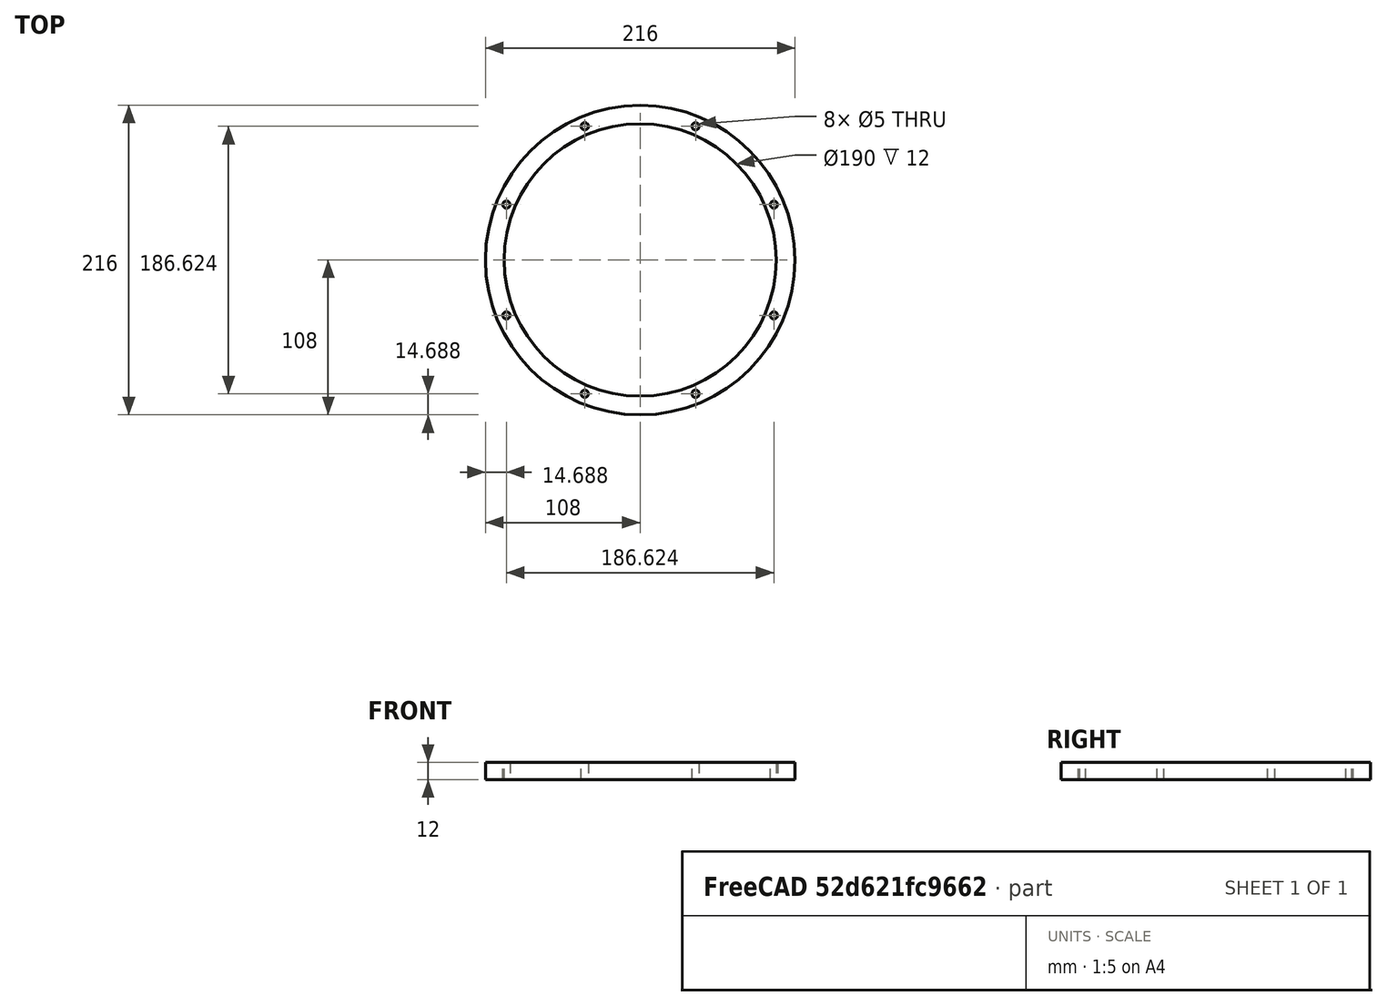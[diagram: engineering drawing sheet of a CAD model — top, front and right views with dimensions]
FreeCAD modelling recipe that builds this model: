
FCSTD DOCUMENT  (FreeCAD 0.19R24276 (Git))
Label: Out_gear_holder_for_CNC_H12_middle_parts
License: All rights reserved
LicenseURL: http://en.wikipedia.org/wiki/All_rights_reserved
objects: Sketcher::SketchObject×1, PartDesign::Pad×1, PartDesign::Body×1
note: 4 computed .brp shape members not serialized (recipe doc carries the construction recipe); baked Part::Feature solids carry a one-line shape summary decoded from their .brp

FEATURE [Sketcher::SketchObject] Sketch001  label="Sketch001_d190_d216"
  FullyConstrained = false
  MapMode = 5
  Placement = pos=(0,0,0) rot=(1,0,0;3.14159rad)
  sketch-geometry (20):
    g0: Circle CenterX=0 CenterY=0 CenterZ=0 NormalX=0 NormalY=0 NormalZ=1 AngleXU=0 Radius=95
    g1: Circle CenterX=0 CenterY=0 CenterZ=0 NormalX=0 NormalY=0 NormalZ=1 AngleXU=0 Radius=95
    g2: Circle CenterX=0 CenterY=0 CenterZ=0 NormalX=0 NormalY=0 NormalZ=1 AngleXU=0 Radius=108
    g3: Circle CenterX=0 CenterY=0 CenterZ=0 NormalX=0 NormalY=0 NormalZ=1 AngleXU=0 Radius=101
    g4: LineSegment StartX=0 StartY=0 StartZ=0 EndX=93.3118 EndY=38.651 EndZ=0
    g5: LineSegment StartX=0 StartY=0 StartZ=0 EndX=-93.3118 EndY=38.651 EndZ=0
    g6: LineSegment StartX=0 StartY=0 StartZ=0 EndX=-93.3118 EndY=-38.651 EndZ=0
    g7: LineSegment StartX=0 StartY=0 StartZ=0 EndX=38.651 EndY=93.3118 EndZ=0
    g8: LineSegment StartX=0 StartY=0 StartZ=0 EndX=-38.651 EndY=-93.3118 EndZ=0
    g9: LineSegment StartX=0 StartY=0 StartZ=0 EndX=-38.651 EndY=93.3118 EndZ=0
    g10: LineSegment StartX=0 StartY=0 StartZ=0 EndX=38.651 EndY=-93.3118 EndZ=0
    g11: LineSegment StartX=0 StartY=0 StartZ=0 EndX=93.3118 EndY=-38.651 EndZ=0
    g12: Circle CenterX=38.651 CenterY=93.3118 CenterZ=0 NormalX=0 NormalY=0 NormalZ=1 AngleXU=0 Radius=2.5
    g13: Circle CenterX=93.3118 CenterY=38.651 CenterZ=0 NormalX=0 NormalY=0 NormalZ=1 AngleXU=0 Radius=2.5
    g14: Circle CenterX=93.3118 CenterY=-38.651 CenterZ=0 NormalX=0 NormalY=0 NormalZ=1 AngleXU=0 Radius=2.5
    g15: Circle CenterX=38.651 CenterY=-93.3118 CenterZ=0 NormalX=0 NormalY=0 NormalZ=1 AngleXU=0 Radius=2.5
    g16: Circle CenterX=-38.651 CenterY=93.3118 CenterZ=0 NormalX=0 NormalY=0 NormalZ=1 AngleXU=0 Radius=2.5
    g17: Circle CenterX=-93.3118 CenterY=38.651 CenterZ=0 NormalX=0 NormalY=0 NormalZ=1 AngleXU=0 Radius=2.5
    g18: Circle CenterX=-93.3118 CenterY=-38.651 CenterZ=0 NormalX=0 NormalY=0 NormalZ=1 AngleXU=0 Radius=2.5
    g19: Circle CenterX=-38.651 CenterY=-93.3118 CenterZ=0 NormalX=0 NormalY=0 NormalZ=1 AngleXU=0 Radius=2.5
  constraints (44):
    c: Coincident(g0,g-1)
    c: Diameter(g0) = 190
    c: Coincident(g1,g0)
    c: Diameter(g1) = 190
    c: Coincident(g2,g1)
    c: Diameter(g2) = 216
    c: Coincident(g3,g1)
    c: Diameter(g3) = 202
    c: Coincident(g4,g1)
    c: Coincident(g5,g1)
    c: Coincident(g6,g1)
    c: Parallel(g6,g4)
    c: Coincident(g7,g1)
    c: Coincident(g8,g1)
    c: Parallel(g8,g7)
    c: Coincident(g9,g1)
    c: Coincident(g10,g1)
    c: Parallel(g10,g9)
    c: PointOnObject(g7,g3)
    c: PointOnObject(g4,g3)
    c: PointOnObject(g9,g3)
    c: PointOnObject(g5,g3)
    c: PointOnObject(g6,g3)
    c: PointOnObject(g8,g3)
    c: PointOnObject(g10,g3)
    c: Coincident(g11,g1)
    c: Parallel(g5,g11)
    c: PointOnObject(g11,g3)
    c: Angle(g-1,g4) = 0.392699
    c: Angle(g4,g7) = 0.785398
    c: Angle(g11,g-1) = 0.392699
    c: Angle(g10,g11) = 0.785398
    c: Coincident(g12,g7)
    c: Coincident(g13,g4)
    c: Coincident(g14,g11)
    c: Coincident(g15,g10)
    c: Diameter(g15) = 5
    c: Equal(g15,g14)
    c: Equal(g15,g13)
    c: Equal(g15,g12)
    c: Diameter(g19) = 5
    c: Equal(g19,g18)
    c: Equal(g19,g17)
    c: Equal(g19,g16)
FEATURE [PartDesign::Pad] Pad  label="Pad_H12"
  Direction = (1,1,1)
  Length = 12
  Length2 = 100
  Placement = pos=(0,0,0) rot=(1,0,0;3.14159rad)
  Profile = -> Sketch001
  Type = 0
FEATURE [PartDesign::Body] Body
  Group = -> [Sketch001,Pad]
  Origin = -> Origin
  Tip = -> Pad
